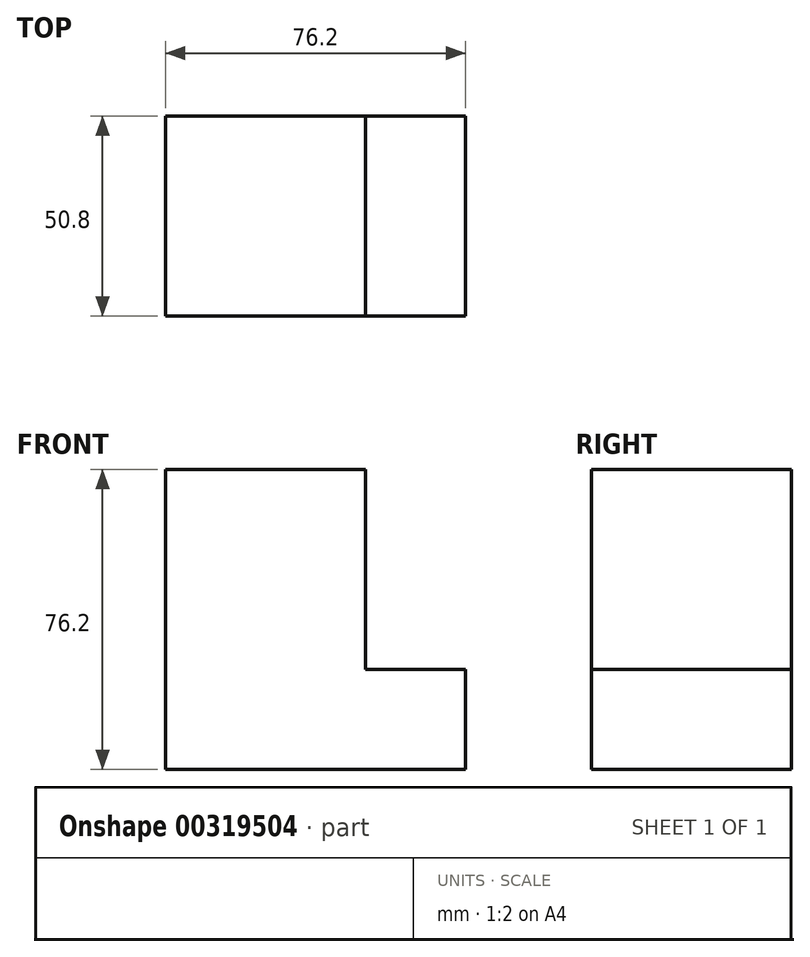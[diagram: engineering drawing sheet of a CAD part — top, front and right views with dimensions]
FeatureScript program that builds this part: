
annotation { "Feature Type Name" : "Feature", "Feature Type Description" : "" }
export const myFeature = defineFeature(function(context is Context, id is Id, definition is map)
    precondition{}
    {
        {
            var Q0;
            Q0=qCreatedBy(makeId("Front.planeOp"),FACE);
            var sketch = newSketch(context, id + "F0", { "sketchPlane" : qUnion([Q0])});
            skLineSegment(sketch, "E0", {"start": v(-37.14, -45.34) * mm, "end": v(39.06, -45.34) * mm});
            skLineSegment(sketch, "E1", {"start": v(39.06, -45.34) * mm, "end": v(39.06, -19.94) * mm});
            skLineSegment(sketch, "E2", {"start": v(39.06, -19.94) * mm, "end": v(13.66, -19.94) * mm});
            skLineSegment(sketch, "E3", {"start": v(13.66, -19.94) * mm, "end": v(13.66, 30.86) * mm});
            skLineSegment(sketch, "E4", {"start": v(13.66, 30.86) * mm, "end": v(-37.14, 30.86) * mm});
            skLineSegment(sketch, "E5", {"start": v(-37.14, 30.86) * mm, "end": v(-37.14, -45.34) * mm});
            skSolve(sketch);
        }
        {
            var Q0;
            Q0=makeQuery(id+"F0.imprint","IMPRINT",FACE,{"disambiguationData":[TD([[makeQuery(id+"F0.imprint","IMPRINT",EDGE,{"derivedFrom":sQuery(id+"F0.wireOp",EDGE,"E0")}),1.0]])]});
            extrude(context, id + "F1", {"entities" : qUnion([Q0]), "depth" : 50.8 * mm});
        }
    });
